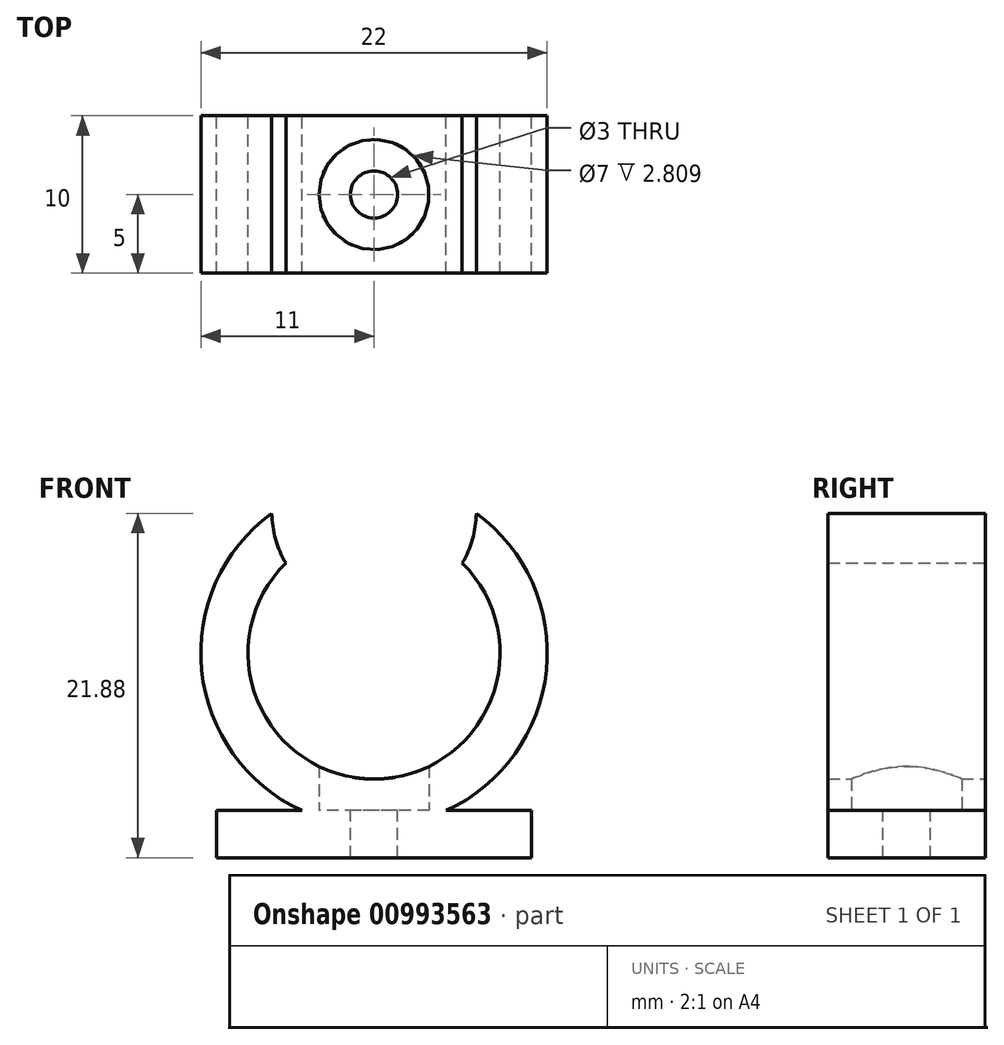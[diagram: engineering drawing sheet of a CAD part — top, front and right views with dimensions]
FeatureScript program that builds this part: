
annotation { "Feature Type Name" : "Feature", "Feature Type Description" : "" }
export const myFeature = defineFeature(function(context is Context, id is Id, definition is map)
    precondition{}
    {
        {
            var Q0;
            Q0=qCreatedBy(makeId("Top.planeOp"),FACE);
            var sketch = newSketch(context, id + "F0", { "sketchPlane" : qUnion([Q0])});
            skLineSegment(sketch, "E0.bottom", {"start": v(-10, -5) * mm, "end": v(10, -5) * mm});
            skLineSegment(sketch, "E0.top", {"start": v(-10, 5) * mm, "end": v(10, 5) * mm});
            skLineSegment(sketch, "E0.left", {"start": v(-10, -5) * mm, "end": v(-10, 5) * mm});
            skLineSegment(sketch, "E0.right", {"start": v(10, -5) * mm, "end": v(10, 5) * mm});
            skPoint(sketch, "E0.middle", {"position": v(0, 0) * mm});
            skSolve(sketch);
        }
        {
            var Q0;
            Q0=makeQuery(id+"F0.imprint","IMPRINT",FACE,{"disambiguationData":[TD([[makeQuery(id+"F0.imprint","IMPRINT",EDGE,{"derivedFrom":sQuery(id+"F0.wireOp",EDGE,"E0.bottom")}),1.0]])]});
            extrude(context, id + "F1", {"entities" : qUnion([Q0]), "depth" : 3 * mm, "offsetDistance" : 25 * mm});
        }
        {
            var Q0;
            Q0=qCreatedBy(makeId("Front.planeOp"),FACE);
            var sketch = newSketch(context, id + "F2", { "sketchPlane" : qUnion([Q0])});
            skArc(sketch, "E1", {"start": v(-5.6, 18.71) * mm, "mid": v(0, 5) * mm, "end": v(5.6, 18.71) * mm});
            skArc(sketch, "E2.0", {"start": v(-6.5, 21.88) * mm, "mid": v(0, 2) * mm, "end": v(6.5, 21.88) * mm});
            skArc(sketch, "E3", {"start": v(5.6, 18.71) * mm, "mid": v(6.25, 20.24) * mm, "end": v(6.5, 21.88) * mm});
            skArc(sketch, "E4.trimOffspring", {"start": v(-6.5, 21.88) * mm, "mid": v(-6.25, 20.24) * mm, "end": v(-5.6, 18.71) * mm});
            skSolve(sketch);
        }
        {
            var Q0;
            Q0=makeQuery(id+"F2.imprint","IMPRINT",FACE,{"disambiguationData":[TD([[makeQuery(id+"F2.imprint","IMPRINT",EDGE,{"derivedFrom":sQuery(id+"F2.wireOp",EDGE,"E1")}),-1.0]])]});
            extrude(context, id + "F3", {"entities" : qUnion([Q0]), "operationType" : NewBodyOperationType.ADD, "endBound" : BoundingType.SYMMETRIC, "depth" : 10 * mm, "offsetDistance" : 25 * mm});
        }
        {
            var Q0;
            {var subQ0=sQuery(id+"F0.wireOp",EDGE,"E0.left");var subQ1=sQuery(id+"F0.wireOp",EDGE,"E0.top");var subQ6=sQuery(id+"F0.wireOp",EDGE,"E0.bottom");Q0=makeQuery(id+"F3.boolean.opBoolean","SPLIT",FACE,{"disambiguationData":[TD([makeQuery(id+"F1.opExtrude","SWEPT_FACE",FACE,{"disambiguationData":[OSD([subQ0])]})])],"derivedFrom":makeQuery(id+"F1.opExtrude","CAP_FACE",FACE,{"disambiguationData":[OSD([subQ6,subQ1,subQ0,sQuery(id+"F0.wireOp",EDGE,"E0.right")])],"isStart":false})});}
            var sketch = newSketch(context, id + "F4", { "sketchPlane" : qUnion([Q0])});
            skCircle(sketch, "E5", {"center": v(0, 0) * mm, "radius": 1.5 * mm});
            skSolve(sketch);
        }
        {
            var Q0;
            Q0 = qSketchRegion(id + "F4", true);
            extrude(context, id + "F5", {"entities" : qUnion([Q0]), "operationType" : NewBodyOperationType.REMOVE, "endBound" : BoundingType.SYMMETRIC, "oppositeDirection" : true, "depth" : 25 * mm, "offsetDistance" : 25 * mm});
        }
        {
            var Q0;
            {var subQ0=sQuery(id+"F0.wireOp",EDGE,"E0.left");var subQ1=sQuery(id+"F0.wireOp",EDGE,"E0.top");var subQ6=sQuery(id+"F0.wireOp",EDGE,"E0.bottom");Q0=makeQuery(id+"F3.boolean.opBoolean","SPLIT",FACE,{"disambiguationData":[TD([makeQuery(id+"F1.opExtrude","SWEPT_FACE",FACE,{"disambiguationData":[OSD([subQ0])]})])],"derivedFrom":makeQuery(id+"F1.opExtrude","CAP_FACE",FACE,{"disambiguationData":[OSD([subQ6,subQ1,subQ0,sQuery(id+"F0.wireOp",EDGE,"E0.right")])],"isStart":false})});}
            var sketch = newSketch(context, id + "F6", { "sketchPlane" : qUnion([Q0])});
            skCircle(sketch, "E6", {"center": v(0, 0) * mm, "radius": 3.5 * mm});
            skSolve(sketch);
        }
        {
            var Q0;
            Q0 = qSketchRegion(id + "F6", true);
            extrude(context, id + "F7", {"entities" : qUnion([Q0]), "operationType" : NewBodyOperationType.REMOVE, "depth" : 25 * mm, "offsetDistance" : 25 * mm});
        }
    });
